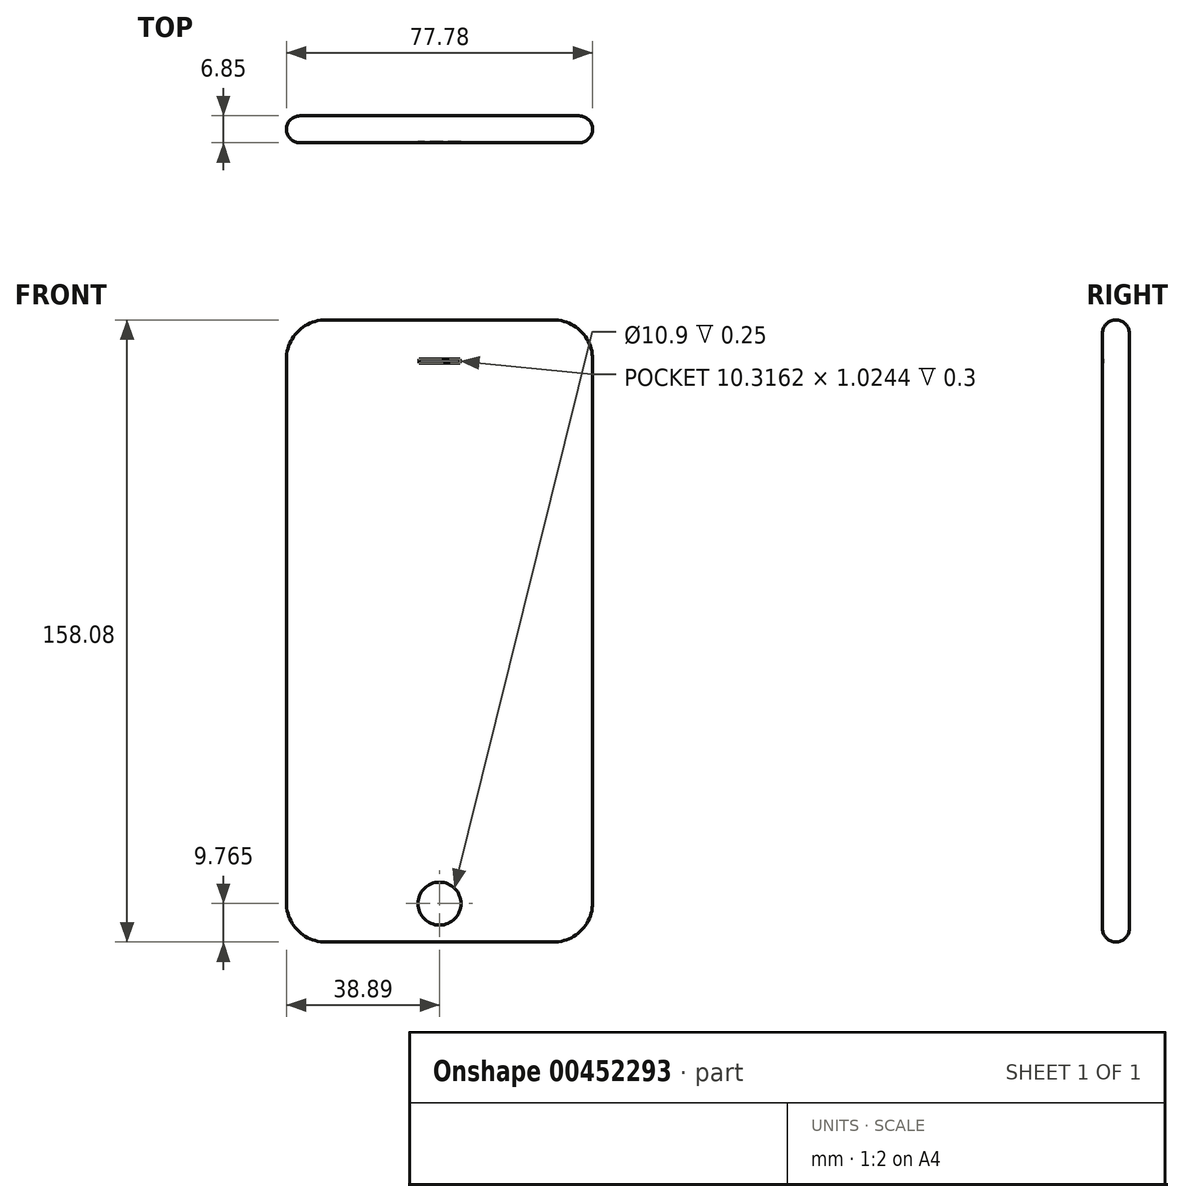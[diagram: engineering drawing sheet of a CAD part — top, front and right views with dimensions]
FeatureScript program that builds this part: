
annotation { "Feature Type Name" : "Feature", "Feature Type Description" : "" }
export const myFeature = defineFeature(function(context is Context, id is Id, definition is map)
    precondition{}
    {
        {
            var Q0;
            Q0=qCreatedBy(makeId("Front.planeOp"),FACE);
            var sketch = newSketch(context, id + "F0", { "sketchPlane" : qUnion([Q0])});
            skLineSegment(sketch, "E0.bottom", {"start": v(28.9, 79.03) * mm, "end": v(-28.9, 79.03) * mm});
            skLineSegment(sketch, "E0.top", {"start": v(28.9, -79.03) * mm, "end": v(-28.9, -79.03) * mm});
            skLineSegment(sketch, "E0.left", {"start": v(38.9, 69.03) * mm, "end": v(38.9, -69.03) * mm});
            skLineSegment(sketch, "E0.right", {"start": v(-38.9, 69.03) * mm, "end": v(-38.9, -69.03) * mm});
            skPoint(sketch, "E0.middle", {"position": v(0, 0) * mm});
            skPoint(sketch, "E1.visualSharp", {"position": v(-38.9, 79.03) * mm});
            skArc(sketch, "E1.filletArc", {"start": v(-28.9, 79.03) * mm, "mid": v(-35.97, 76.1) * mm, "end": v(-38.9, 69.03) * mm});
            skPoint(sketch, "E2.visualSharp", {"position": v(38.9, 79.03) * mm});
            skArc(sketch, "E2.filletArc", {"start": v(38.9, 69.03) * mm, "mid": v(35.97, 76.1) * mm, "end": v(28.9, 79.04) * mm});
            skPoint(sketch, "E3.visualSharp", {"position": v(38.9, -79.03) * mm});
            skArc(sketch, "E3.filletArc", {"start": v(28.9, -79.03) * mm, "mid": v(35.97, -76.1) * mm, "end": v(38.9, -69.03) * mm});
            skPoint(sketch, "E4.visualSharp", {"position": v(-38.9, -79.03) * mm});
            skArc(sketch, "E4.filletArc", {"start": v(-38.9, -69.03) * mm, "mid": v(-35.97, -76.1) * mm, "end": v(-28.9, -79.03) * mm});
            skSolve(sketch);
        }
        {
            var Q0;
            Q0 = qSketchRegion(id + "F0", true);
            extrude(context, id + "F1", {"entities" : qUnion([Q0]), "depth" : 6.85 * mm});
        }
        {
            var Q0;
            Q0=makeQuery(id+"F1.opExtrude","CAP_EDGE",EDGE,{"disambiguationData":[OSD([sQuery(id+"F0.wireOp",EDGE,"E0.bottom")])],"isStart":false});
            var Q1;
            Q1=makeQuery(id+"F1.opExtrude","CAP_EDGE",EDGE,{"disambiguationData":[OSD([sQuery(id+"F0.wireOp",EDGE,"E0.bottom")])],"isStart":true});
            fillet(context, id + "F2", {"entities" : qUnion([Q0, Q1]), "radius" : 3.42 * mm, "tangentPropagation" : true, "allowEdgeOverflow" : false});
        }
        {
            var Q0;
            Q0=makeQuery(id+"F1.opExtrude","CAP_FACE",FACE,{"disambiguationData":[OSD([sQuery(id+"F0.wireOp",EDGE,"E0.bottom"),sQuery(id+"F0.wireOp",EDGE,"E0.top"),sQuery(id+"F0.wireOp",EDGE,"E0.left"),sQuery(id+"F0.wireOp",EDGE,"E0.right"),sQuery(id+"F0.wireOp",EDGE,"E1.filletArc"),sQuery(id+"F0.wireOp",EDGE,"E2.filletArc"),sQuery(id+"F0.wireOp",EDGE,"E3.filletArc"),sQuery(id+"F0.wireOp",EDGE,"E4.filletArc")])],"isStart":false});
            var sketch = newSketch(context, id + "F3", { "sketchPlane" : qUnion([Q0])});
            skLineSegment(sketch, "E5.bottom", {"start": v(34.44, 60.77) * mm, "end": v(-34.44, 60.77) * mm});
            skLineSegment(sketch, "E5.top", {"start": v(34.44, -60.77) * mm, "end": v(-34.44, -60.77) * mm});
            skLineSegment(sketch, "E5.left", {"start": v(34.44, 60.77) * mm, "end": v(34.44, -60.77) * mm});
            skLineSegment(sketch, "E5.right", {"start": v(-34.44, 60.77) * mm, "end": v(-34.44, -60.77) * mm});
            skPoint(sketch, "E5.middle", {"position": v(0, 0) * mm});
            skSolve(sketch);
        }
        {
            var Q0;
            Q0=makeQuery(id+"F3.imprint","IMPRINT",FACE,{"disambiguationData":[TD([[makeQuery(id+"F3.imprint","IMPRINT",EDGE,{"derivedFrom":sQuery(id+"F3.wireOp",EDGE,"E5.bottom")}),-1.0]])]});
            var sketch = newSketch(context, id + "F4", { "sketchPlane" : qUnion([Q0])});
            skCircle(sketch, "E6", {"center": v(0, -69.27) * mm, "radius": 5.45 * mm});
            skSolve(sketch);
        }
        {
            var Q0;
            Q0 = qSketchRegion(id + "F4", true);
            var Q1;
            Q1=sQuery(id+"F4.wireOp",EDGE,"E6");
            extrude(context, id + "F5", {"entities" : qUnion([Q0]), "operationType" : NewBodyOperationType.REMOVE, "surfaceEntities" : qUnion([Q1]), "oppositeDirection" : true, "depth" : 0.25 * mm});
        }
        {
            var Q0;
            Q0=makeQuery(id+"F3.imprint","IMPRINT",FACE,{"disambiguationData":[TD([[makeQuery(id+"F3.imprint","IMPRINT",EDGE,{"derivedFrom":sQuery(id+"F3.wireOp",EDGE,"E5.bottom")}),-1.0]])]});
            var sketch = newSketch(context, id + "F6", { "sketchPlane" : qUnion([Q0])});
            skLineSegment(sketch, "E7.bottom", {"start": v(5.16, 69.12) * mm, "end": v(-5.16, 69.12) * mm});
            skLineSegment(sketch, "E7.top", {"start": v(5.16, 68.1) * mm, "end": v(-5.16, 68.1) * mm});
            skLineSegment(sketch, "E7.left", {"start": v(5.16, 69.12) * mm, "end": v(5.16, 68.1) * mm});
            skLineSegment(sketch, "E7.right", {"start": v(-5.16, 69.12) * mm, "end": v(-5.16, 68.1) * mm});
            skPoint(sketch, "E7.middle", {"position": v(0, 68.6) * mm});
            skSolve(sketch);
        }
        {
            var Q0;
            Q0 = qSketchRegion(id + "F6", true);
            extrude(context, id + "F7", {"entities" : qUnion([Q0]), "operationType" : NewBodyOperationType.REMOVE, "oppositeDirection" : true, "depth" : 0.3 * mm});
        }
    });
